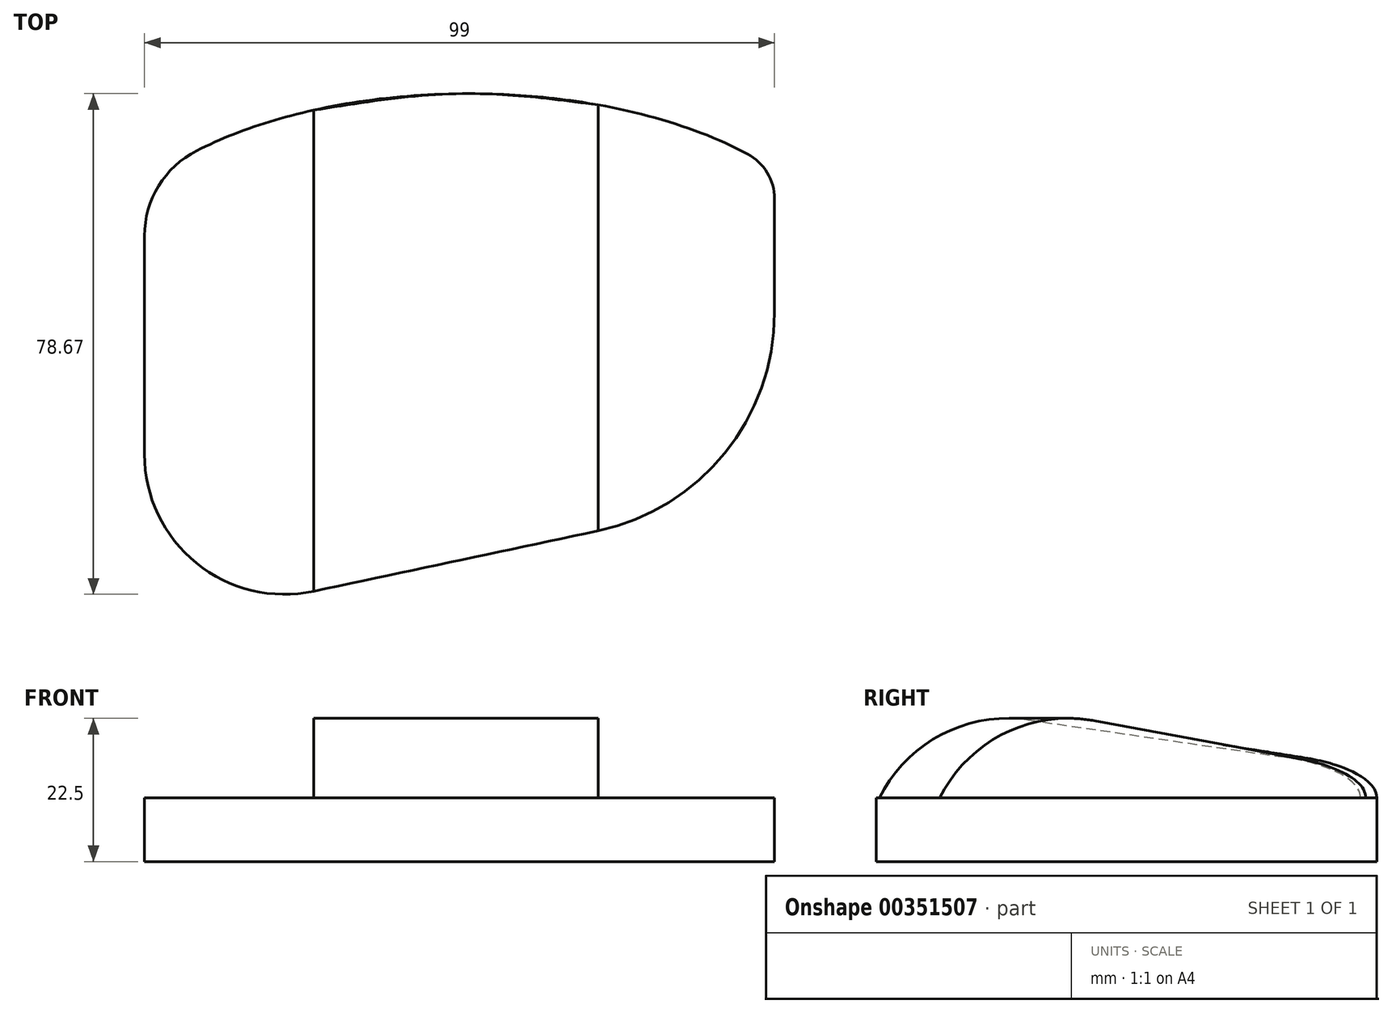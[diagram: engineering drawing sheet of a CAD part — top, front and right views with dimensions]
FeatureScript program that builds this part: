
annotation { "Feature Type Name" : "Feature", "Feature Type Description" : "" }
export const myFeature = defineFeature(function(context is Context, id is Id, definition is map)
    precondition{}
    {
        {
            var Q0;
            Q0=qCreatedBy(makeId("Top.planeOp"),FACE);
            var sketch = newSketch(context, id + "F0", { "sketchPlane" : qUnion([Q0])});
            skLineSegment(sketch, "E0", {"start": v(-67.26, 20) * mm, "end": v(93.2, 20) * mm, "construction": true});
            skLineSegment(sketch, "E1", {"start": v(48, 52.31) * mm, "end": v(48, 20) * mm, "construction": true});
            skLineSegment(sketch, "E2", {"start": v(-51, -43.52) * mm, "end": v(-51, -43) * mm, "construction": true});
            skLineSegment(sketch, "E3", {"start": v(-69.9, -43) * mm, "end": v(93.42, -43) * mm, "construction": true});
            skLineSegment(sketch, "E4", {"start": v(0, 30) * mm, "end": v(33.85, 30) * mm, "construction": true});
            skLineSegment(sketch, "E5", {"start": v(0, -43) * mm, "end": v(-24.43, -48.2) * mm});
            skLineSegment(sketch, "E6", {"start": v(0, -43) * mm, "end": v(20.28, -38.7) * mm});
            skLineSegment(sketch, "E7.trimOffspring", {"start": v(-51, 20) * mm, "end": v(-51, 63.74) * mm, "construction": true});
            skLineSegment(sketch, "E8.trimOffspring", {"start": v(-51, -26.67) * mm, "end": v(-51, 15.8) * mm});
            skLineSegment(sketch, "E9.trimOffspring", {"start": v(48, -18) * mm, "end": v(48, -42.42) * mm, "construction": true});
            skLineSegment(sketch, "E10.trimOffspring", {"start": v(48, 18) * mm, "end": v(48, -4.45) * mm});
            skArc(sketch, "E11.trimOffspring", {"start": v(20.28, -38.7) * mm, "mid": v(40.2, -26.48) * mm, "end": v(48, -4.45) * mm});
            skArc(sketch, "E12.trimOffspring", {"start": v(-51, -26.67) * mm, "mid": v(-42.85, -43.77) * mm, "end": v(-24.43, -48.2) * mm});
            skEllipticalArc(sketch, "E13.trimOffspring", {});
            const initialGuessF0  = {"E13.trimOffspring": [0, 0, 1, 0, 0.06, 0.03, 0.6435011087932844, 2.586781620609722]};
            skSetInitialGuess(sketch, initialGuessF0);
            skSolve(sketch);
        }
        {
            var Q0;
            Q0=makeQuery(id+"F0.imprint","IMPRINT",FACE,{"disambiguationData":[TD([[makeQuery(id+"F0.imprint","IMPRINT",EDGE,{"derivedFrom":sQuery(id+"F0.wireOp",EDGE,"E5")}),-1.0]])]});
            extrude(context, id + "F1", {"entities" : qUnion([Q0]), "endBound" : BoundingType.SYMMETRIC, "depth" : 10 * mm});
        }
        {
            var Q0;
            Q0=makeQuery(id+"F1.opExtrude","SWEPT_EDGE",EDGE,{"disambiguationData":[OSD([sQuery(id+"F8CPoCA9Al2ZOIw_0.wireOp",EDGE,"5vuCZDCt-Mtiv-Zeuv-8Zjm-snGLHJwt43m1"),sQuery(id+"F8CPoCA9Al2ZOIw_0.wireOp",EDGE,"6e6135b4-3758-407c-90e4-0be94a5ea944.trimOffspring")])]});
            var Q1;
            Q1=makeQuery(id+"F1.opExtrude","SWEPT_EDGE",EDGE,{"disambiguationData":[OSD([sQuery(id+"F8CPoCA9Al2ZOIw_0.wireOp",EDGE,"y53CQRHN-86y9-WdRm-9xJK-u0wu57UlCTpn"),sQuery(id+"F8CPoCA9Al2ZOIw_0.wireOp",EDGE,"ytrkG5K4-qv7W-ofgF-ZHXv-SdK9MCqp6B0v")])]});
            var Q2;
            Q2=makeQuery(id+"F1.opExtrude","SWEPT_EDGE",EDGE,{"disambiguationData":[OSD([sQuery(id+"F0.wireOp",EDGE,"E10.trimOffspring"),sQuery(id+"F0.wireOp",EDGE,"E13.trimOffspring")])]});
            fillet(context, id + "F2", {"entities" : qUnion([Q0, Q1, Q2]), "radius" : 8 * mm, "tangentPropagation" : true, "allowEdgeOverflow" : false});
        }
        {
            var Q0;
            Q0=makeQuery(id+"F1.opExtrude","SWEPT_EDGE",EDGE,{"disambiguationData":[OSD([sQuery(id+"F0.wireOp",EDGE,"E8.trimOffspring"),sQuery(id+"F0.wireOp",EDGE,"E13.trimOffspring")])]});
            var Q1;
            Q1=makeQuery(id+"F1.opExtrude","SWEPT_EDGE",EDGE,{"disambiguationData":[OSD([sQuery(id+"F8CPoCA9Al2ZOIw_0.wireOp",EDGE,"gdmlw1VD-prgP-LAi1-7Qk0-soYjR7bTrSSM"),sQuery(id+"F8CPoCA9Al2ZOIw_0.wireOp",EDGE,"6e6135b4-3758-407c-90e4-0be94a5ea944.trimOffspring")])]});
            fillet(context, id + "F3", {"entities" : qUnion([Q0, Q1]), "radius" : 15 * mm, "tangentPropagation" : true, "allowEdgeOverflow" : false});
        }
        {
            var Q0;
            Q0=qCreatedBy(makeId("Right.planeOp"),FACE);
            var sketch = newSketch(context, id + "F4", { "sketchPlane" : qUnion([Q0])});
            skEllipticalArc(sketch, "E14", {});
            skLineSegment(sketch, "E15", {"start": v(-18.28, 17.03) * mm, "end": v(18.09, 11.4) * mm});
            skArc(sketch, "E16.trimOffspring", {"start": v(-18.28, 17.03) * mm, "mid": v(-32.7, 15.23) * mm, "end": v(-43, 5) * mm});
            skLineSegment(sketch, "E17", {"start": v(30, 5) * mm, "end": v(-43, 5) * mm});
            const initialGuessF4  = {"E14": [0.01, 0.005, 1, 0, 0.02, 0.007, 0, 1.1544241880937842]};
            skSetInitialGuess(sketch, initialGuessF4);
            skSolve(sketch);
        }
        {
            var Q0;
            Q0=makeQuery(id+"F1.opExtrude","SWEPT_EDGE",EDGE,{"disambiguationData":[OSD([sQuery(id+"F0.wireOp",EDGE,"E5"),sQuery(id+"F0.wireOp",EDGE,"E12.trimOffspring")])]});
            cPlane(context, id + "F5", {"entities" : qUnion([Q0]), "cplaneType" : CPlaneType.LINE_ANGLE, "offset" : 25.57 * mm, "angle" : 180 * degree, "oppositeDirection" : true, "width" : 150 * mm, "height" : 150 * mm});
        }
        {
            var Q0;
            Q0=qCreatedBy(id+"F5.planeOp",FACE);
            var sketch = newSketch(context, id + "F6", { "sketchPlane" : qUnion([Q0])});
            skLineSegment(sketch, "E18", {"start": v(-22.85, -5) * mm, "end": v(-22.85, 27.95) * mm, "construction": true});
            skLineSegment(sketch, "E19.0", {"start": v(27.4, -5) * mm, "end": v(27.4, 5) * mm});
            skLineSegment(sketch, "E20.0", {"start": v(-48.2, 5) * mm, "end": v(-48.2, -5) * mm});
            skLineSegment(sketch, "E21", {"start": v(-48.2, 5) * mm, "end": v(27.4, 5) * mm, "construction": true});
            skLineSegment(sketch, "E22", {"start": v(-28.02, 5) * mm, "end": v(-63.42, 5) * mm, "construction": true});
            skLineSegment(sketch, "E23", {"start": v(-24.8, 17.27) * mm, "end": v(15.08, 11.46) * mm});
            skArc(sketch, "E24", {"start": v(-24.8, 17.27) * mm, "mid": v(-38.48, 14.93) * mm, "end": v(-48.2, 5) * mm});
            skPoint(sketch, "E24.first.point", {"position": v(-39.21, 14.53) * mm});
            skPoint(sketch, "E24.second.point", {"position": v(-11.7, 10.48) * mm});
            skPoint(sketch, "E24.third.point", {"position": v(-17.24, -24.74) * mm});
            skEllipticalArc(sketch, "E25.trimOffspring", {});
            skLineSegment(sketch, "E26", {"start": v(-48.2, 5) * mm, "end": v(27.4, 5) * mm});
            const initialGuessF6  = {"E25.trimOffspring": [0.007401520570184464, 0.005, 1, 0, 0.02, 0.007, 0, 1.1768199942119344]};
            skSetInitialGuess(sketch, initialGuessF6);
            skSolve(sketch);
        }
        {
            var Q0;
            Q0=makeQuery(id+"F1.opExtrude","SWEPT_EDGE",EDGE,{"disambiguationData":[OSD([sQuery(id+"F0.wireOp",EDGE,"E6"),sQuery(id+"F0.wireOp",EDGE,"E11.trimOffspring")])]});
            cPlane(context, id + "F7", {"entities" : qUnion([Q0]), "cplaneType" : CPlaneType.LINE_ANGLE, "offset" : 20.13 * mm, "angle" : 180 * degree, "width" : 150 * mm, "height" : 150 * mm});
        }
        {
            var Q0;
            Q0=qCreatedBy(id+"F7.planeOp",FACE);
            var sketch = newSketch(context, id + "F8", { "sketchPlane" : qUnion([Q0])});
            skLineSegment(sketch, "E27.0", {"start": v(28.23, 5) * mm, "end": v(-38.7, 5) * mm});
            skLineSegment(sketch, "E28.0", {"start": v(-38.7, -5) * mm, "end": v(28.23, -5) * mm, "construction": true});
            skLineSegment(sketch, "E29", {"start": v(-14.43, 17.12) * mm, "end": v(17.6, 11.19) * mm});
            skEllipticalArc(sketch, "E30.trimOffspring", {});
            skArc(sketch, "E31.trimOffspring", {"start": v(-14.43, 17.12) * mm, "mid": v(-28.6, 15.13) * mm, "end": v(-38.7, 5) * mm});
            const initialGuessF8  = {"E30.trimOffspring": [0.008234938259902094, 0.005, 1, 0, 0.02, 0.007, 0, 1.0837333668589004]};
            skSetInitialGuess(sketch, initialGuessF8);
            skSolve(sketch);
        }
        {
            var Q1;
            Q1=makeQuery(id+"F6.imprint","IMPRINT",FACE,{"disambiguationData":[TD([[makeQuery(id+"F6.imprint","IMPRINT",EDGE,{"derivedFrom":sQuery(id+"F6.wireOp",EDGE,"E23")}),-1.0]])]});
            var Q2;
            Q2=makeQuery(id+"F4.imprint","IMPRINT",FACE,{"disambiguationData":[TD([[makeQuery(id+"F4.imprint","IMPRINT",EDGE,{"derivedFrom":sQuery(id+"F4.wireOp",EDGE,"E14")}),1.0]])]});
            var Q3;
            Q3=makeQuery(id+"F8.imprint","IMPRINT",FACE,{"disambiguationData":[TD([[makeQuery(id+"F8.imprint","IMPRINT",EDGE,{"derivedFrom":sQuery(id+"F8.wireOp",EDGE,"E27.0")}),-1.0]])]});
            loft(context, id + "F9", {"operationType" : NewBodyOperationType.ADD, "sheetProfilesArray" : [{ "sheetProfileEntities" : qUnion([Q1]) }, { "sheetProfileEntities" : qUnion([Q2]) }, { "sheetProfileEntities" : qUnion([Q3]) }]});
        }
    });
